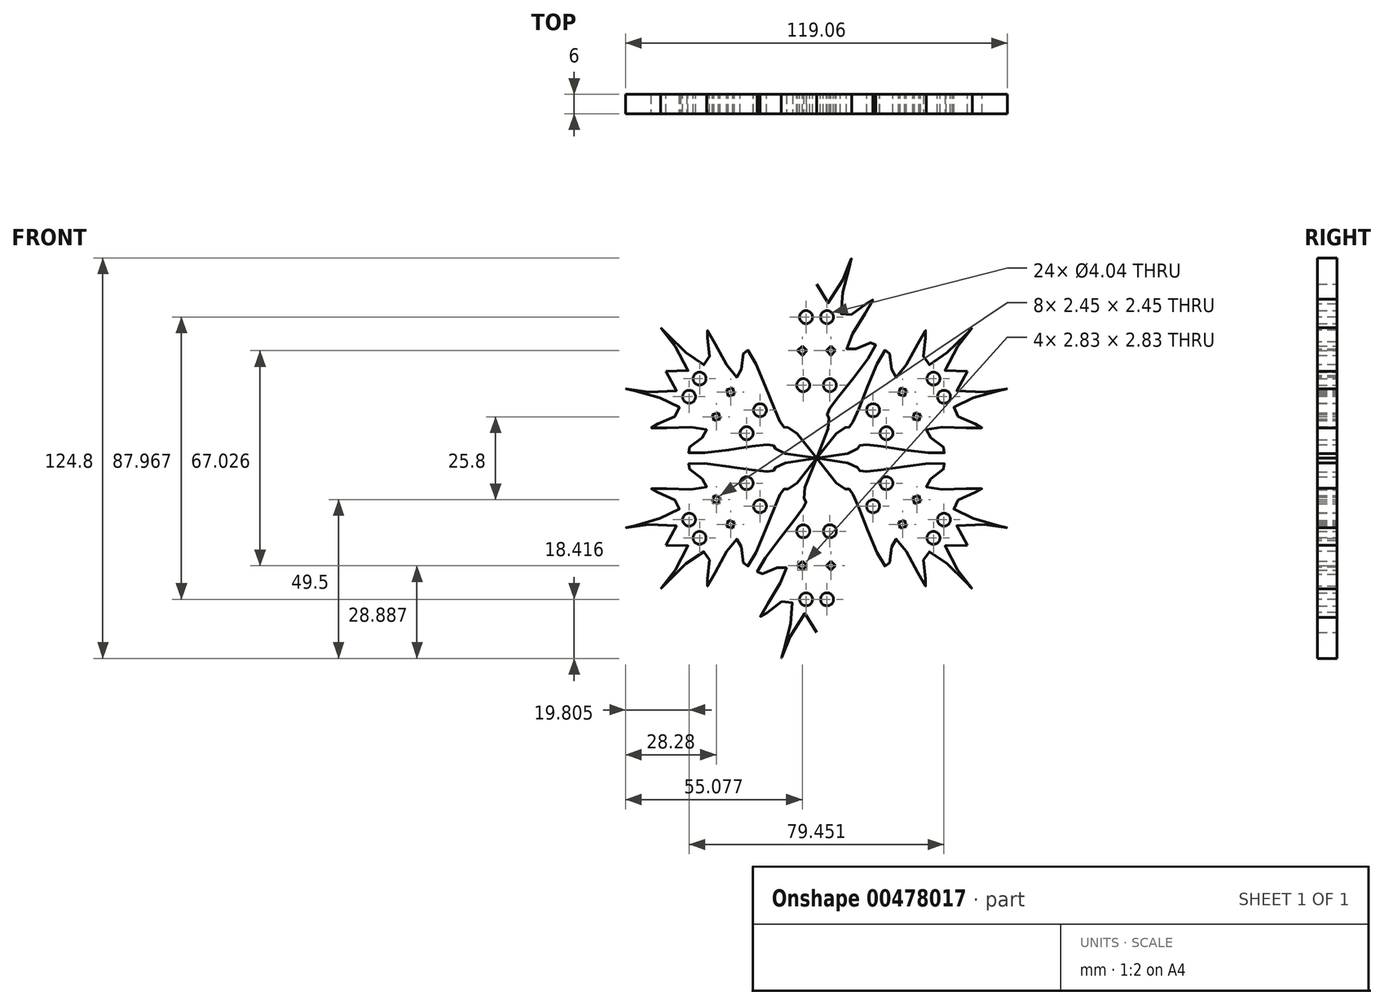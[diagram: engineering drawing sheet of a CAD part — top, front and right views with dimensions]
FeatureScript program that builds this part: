
annotation { "Feature Type Name" : "Feature", "Feature Type Description" : "" }
export const myFeature = defineFeature(function(context is Context, id is Id, definition is map)
    precondition{}
    {
        {
            var Q0;
            Q0=qCreatedBy(makeId("Front.planeOp"),FACE);
            var sketch = newSketch(context, id + "F0", { "sketchPlane" : qUnion([Q0])});
            skLineSegment(sketch, "E0", {"start": v(0, 0) * mm, "end": v(0, 61.65) * mm, "construction": true});
            skFitSpline(sketch, "E1", {"points": [v(0, 54.25) * mm, v(10.75, 61.84) * mm, v(7.93, 44.42) * mm, v(17.5, 49.56) * mm, v(9.47, 33.92) * mm, v(18.17, 36.22) * mm, v(6.61, 18.9) * mm, v(3.3, 13.57) * mm, v(0, 0) * mm], "startDerivative": vector(50.1, -390.34) * mm, "endDerivative": vector(-142.46, -303.97) * mm});
            skCircle(sketch, "E2", {"center": v(3.27, 43.98) * mm, "radius": 2.02 * mm});
            skCircle(sketch, "E3", {"center": v(4.16, 22.76) * mm, "radius": 2.02 * mm});
            skLineSegment(sketch, "E4.bottom", {"start": v(4.45, 34.93) * mm, "end": v(5.87, 33.51) * mm});
            skLineSegment(sketch, "E4.top", {"start": v(3.04, 33.51) * mm, "end": v(4.45, 32.1) * mm});
            skLineSegment(sketch, "E4.left", {"start": v(4.45, 34.93) * mm, "end": v(3.04, 33.51) * mm});
            skLineSegment(sketch, "E4.right", {"start": v(5.87, 33.51) * mm, "end": v(4.45, 32.1) * mm});
            skFitSpline(sketch, "E5.MirrorCS", {"points": [v(0, 54.25) * mm, v(-10.75, 61.84) * mm, v(-7.93, 44.42) * mm, v(-17.5, 49.56) * mm, v(-9.47, 33.92) * mm, v(-18.17, 36.22) * mm, v(-6.61, 18.9) * mm, v(-3.3, 13.57) * mm, v(0, 0) * mm], "startDerivative": vector(-50.1, -390.34) * mm, "endDerivative": vector(142.46, -303.97) * mm});
            skCircle(sketch, "E6.MirrorC", {"center": v(-3.27, 43.98) * mm, "radius": 2.02 * mm});
            skLineSegment(sketch, "E7.MirrorCS", {"start": v(-4.45, 34.93) * mm, "end": v(-3.04, 33.51) * mm});
            skLineSegment(sketch, "E8.MirrorCS", {"start": v(-3.04, 33.51) * mm, "end": v(-4.45, 32.1) * mm});
            skLineSegment(sketch, "E9.MirrorCS", {"start": v(-4.45, 34.93) * mm, "end": v(-5.87, 33.51) * mm});
            skLineSegment(sketch, "E10.MirrorCS", {"start": v(-5.87, 33.51) * mm, "end": v(-4.45, 32.1) * mm});
            skCircle(sketch, "E11.MirrorC", {"center": v(-4.16, 22.76) * mm, "radius": 2.02 * mm});
            skSolve(sketch);
        }
        {
            var Q0;
            Q0=qSketchRegion(id+"F0",true);
            extrude(context, id + "F1", {"entities" : qUnion([Q0]), "depth" : 6 * mm});
        }
        {
            var Q0;
            Q0=qCreatedBy(makeId("Right.planeOp"),FACE);
            var sketch = newSketch(context, id + "F2", { "sketchPlane" : qUnion([Q0])});
            skLineSegment(sketch, "E12", {"start": v(0, 0) * mm, "end": v(-66.9, 0) * mm, "construction": true});
            skSolve(sketch);
        }
        {
            var Q0;
            Q0=makeQuery(id+"F1.opExtrude","SWEPT_BODY",BODY,{"disambiguationData":[OSD([sQuery(id+"F0.wireOp",EDGE,"E1"),sQuery(id+"F0.wireOp",EDGE,"E2"),sQuery(id+"F0.wireOp",EDGE,"E3"),sQuery(id+"F0.wireOp",EDGE,"E4.bottom"),sQuery(id+"F0.wireOp",EDGE,"E4.top"),sQuery(id+"F0.wireOp",EDGE,"E4.left"),sQuery(id+"F0.wireOp",EDGE,"E4.right"),sQuery(id+"F0.wireOp",EDGE,"E5.MirrorCS"),sQuery(id+"F0.wireOp",EDGE,"E6.MirrorC"),sQuery(id+"F0.wireOp",EDGE,"E7.MirrorCS"),sQuery(id+"F0.wireOp",EDGE,"E8.MirrorCS"),sQuery(id+"F0.wireOp",EDGE,"E9.MirrorCS"),sQuery(id+"F0.wireOp",EDGE,"E10.MirrorCS"),sQuery(id+"F0.wireOp",EDGE,"E11.MirrorC")])]});
            var Q1;
            Q1=sQuery(id+"F2.wireOp",EDGE,"E12");
            circularPattern(context, id + "F3", {"entities" : qUnion([Q0]), "axis" : qUnion([Q1]), "angle" : 360 * degree, "instanceCount" : 6, "equalSpace" : true});
        }
    });
